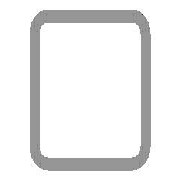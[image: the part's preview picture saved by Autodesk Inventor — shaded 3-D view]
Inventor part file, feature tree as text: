
AUTODESK INVENTOR PART (.ipt)
format: ipt  version: 2024.3 (Build 283343000, 343)  size: 152,576 bytes
history: native  units: mm (DEFAULTED — no unit token found)
features: other x4, plane x2, sketch x2, split x1, extrude x1
ambient origin geometry x8: Origin, YZ Plane, XZ Plane, XY Plane, X Axis, Y Axis, Z Axis, Center Point
bodies: Solid1 (feature_tree), Body (feature_tree)
feature tree (10):
  parser-record x1  (decoder bookkeeping rows leaked as tree rows — omitted from the tree; the rows remain in map.json)
  other  "Driven Length"
  other  "Start Plane"
  other  "End Plane"
  plane  "Work Plane4"
  split  "Split1"
  extrude  "Extrusion2"  TaperAngle=0.0deg  [1 undecoded]
  sketch  "Sketch3"  dims[d3=350.0mm d4=0.0mm]
  plane  "Work Plane3"
  sketch  "Sketch5"  dims[d7=6.0mm d9=100.0mm d11=100.0mm d12=3.0mm d13=-50.0mm d14=300.0mm d15=50.0mm d16=50.0mm d17=90.0deg d18=350.0mm d19=100.0mm d20=10.0mm d21=0.0mm]
note: 1 required parameter value undecoded (feature->parameter linkage not recoverable at this tier; creation-order binding heuristic only, values carry confidence <= 0.55)
